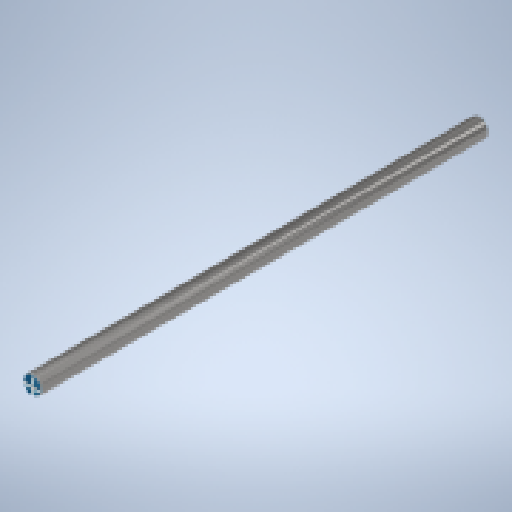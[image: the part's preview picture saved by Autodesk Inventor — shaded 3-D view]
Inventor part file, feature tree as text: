
AUTODESK INVENTOR PART (.ipt)
format: ipt  version: 2025.2 (Build 292293000, 293)  size: 259,584 bytes
history: native  units: mm
features: extrude x1, chamfer x1, sketch x1
ambient origin geometry x8: Origin, YZ Plane, XZ Plane, XY Plane, X Axis, Y Axis, Z Axis, Center Point
bodies: Solid1 (feature_tree)
feature tree (3):
  extrude  "Extrusion1"  Depth=195.0mm TaperAngle=0.0deg
  chamfer  "Chamfer1"  Distance=0.5mm Angle=45.0deg
  sketch  "Sketch1"  dims[d0=8.0mm d1=195.0mm d2=0.0mm d3=0.5mm d4=2.0mm d5=45.0deg]
